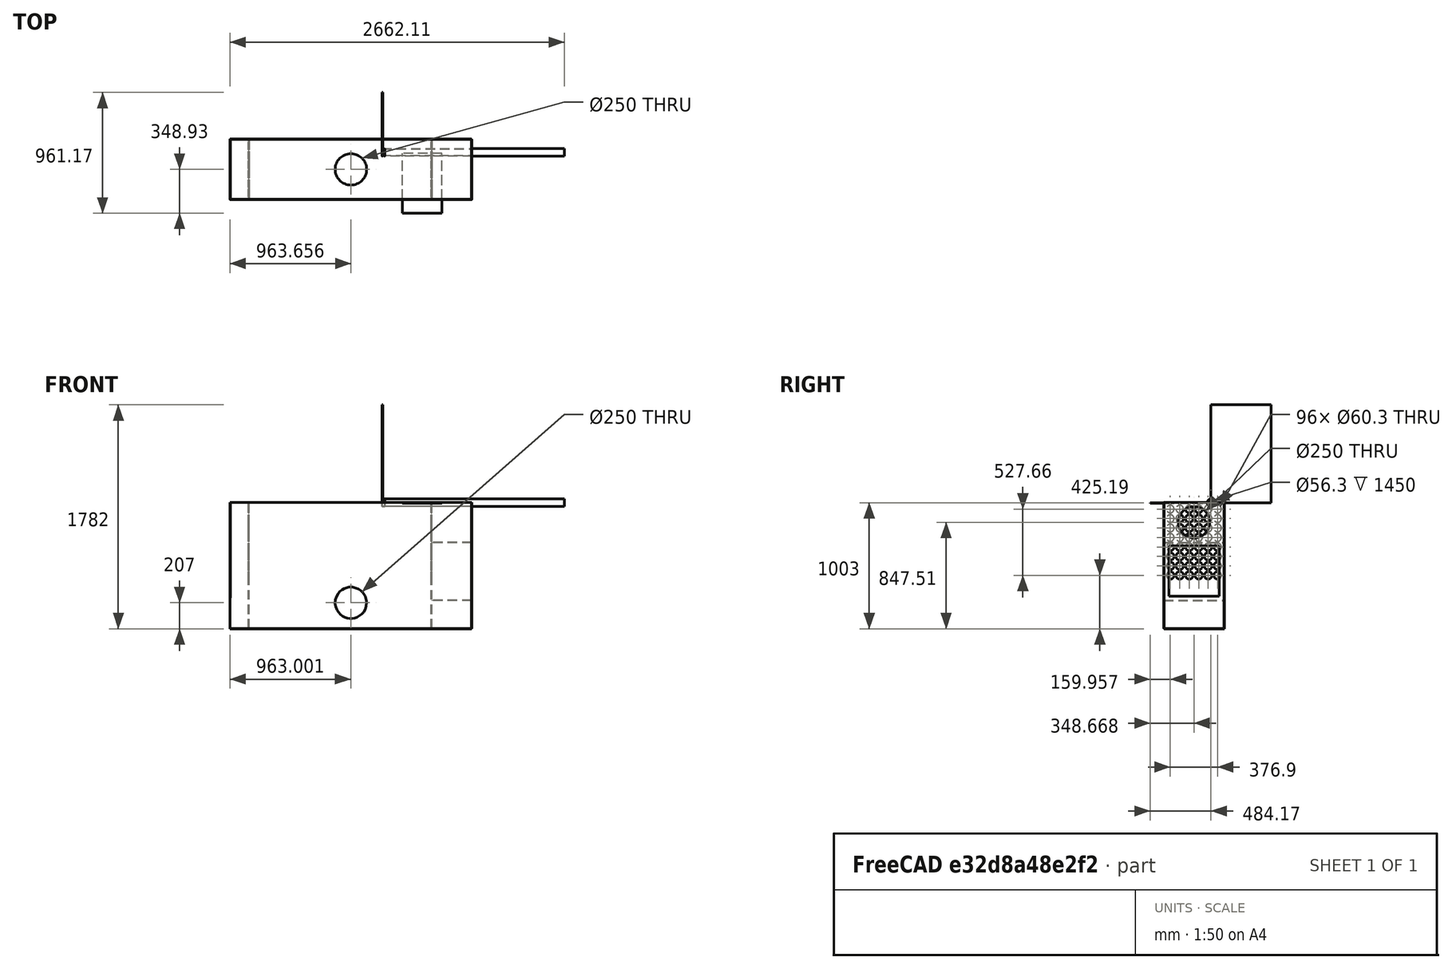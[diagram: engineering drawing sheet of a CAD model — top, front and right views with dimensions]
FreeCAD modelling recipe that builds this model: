
FCSTD DOCUMENT  (FreeCAD 0.19R24291 (Git))
Label: intercambiador_v5
License: All rights reserved
LicenseURL: http://en.wikipedia.org/wiki/All_rights_reserved
objects: TechDraw::DrawViewDimension×29, Part::Box×12, TechDraw::DrawViewPart×9, Part::Cylinder×7, Part::Cut×6, Part::Part2DObjectPython×6, TechDraw::DrawSVGTemplate×5, TechDraw::DrawPage×5, Part::FeaturePython×4, Part::RuledSurface×4, Part::Extrusion×4, Part::Refine×3, Part::MultiFuse×2, TechDraw::DrawHatch×2, Sketcher::SketchObject×1, PartDesign::Pad×1, PartDesign::Body×1
note: 48 computed .brp shape members not serialized (recipe doc carries the construction recipe); baked Part::Feature solids carry a one-line shape summary decoded from their .brp

FEATURE [Sketcher::SketchObject] Sketch
  FullyConstrained = false
  MapMode = 5
  Placement = pos=(0,0,0) rot=(0.57735,0.57735,0.57735;2.0944rad)
  Support = -> [YZ_Plane]
  sketch-geometry (2):
    g0: Circle CenterX=0 CenterY=0 CenterZ=0 NormalX=0 NormalY=0 NormalZ=1 AngleXU=0 Radius=30.15
    g1: Circle CenterX=0 CenterY=0 CenterZ=0 NormalX=0 NormalY=0 NormalZ=1 AngleXU=0 Radius=28.15
  constraints (2):
    c: Diameter(g0) = 60.3
    c: Diameter(g1) = 56.3
FEATURE [PartDesign::Pad] Pad
  AllowMultiFace = false
  Direction = (1,1,1)
  Length = 1450
  Length2 = 100
  Placement = pos=(0,0,0) rot=(0.57735,0.57735,0.57735;2.0944rad)
  Profile = -> Sketch
  Type = 0
FEATURE [PartDesign::Body] Body  label="Caño"
  Group = -> [Sketch,Pad]
  Origin = -> Origin
  Tip = -> Pad
FEATURE [Part::Cylinder] Cylinder  label="Cilindro"
  Angle = 360
  AttacherType = Attacher::AttachEngine3D
  Height = 20
  Placement = pos=(0,0,0) rot=(0,1,0;1.5708rad)
  Radius = 30.15
FEATURE [Part::Box] Box  label="Chapa tubos"
  AttacherType = Attacher::AttachEngine3D
  Height = 779
  Length = 6
  Width = 477
FEATURE [Part::Box] Box001  label="Placa separadora"
  AttacherType = Attacher::AttachEngine3D
  Height = 477
  Length = 3
  Placement = pos=(476.059,-484.167,0) rot=(0.57735,-0.57735,-0.57735;4.18879rad)
  Width = 314
FEATURE [Part::FeaturePython] Array  label="Banco tubos"  # Draft array (typed FeaturePython)
  Angle = 360
  ArrayType = 0
  Axis = (0,0,1)
  Base = -> Body
  Center = (0,0,0)
  Count = 48
  ExpandArray = false
  Fuse = false
  IntervalAxis = (0,0,0)
  IntervalX = (100,0,0)
  IntervalY = (0,75.38,0)
  IntervalZ = (0,0,75.38)
  NumberCircles = 3
  NumberPolar = 5
  NumberX = 1
  NumberY = 6
  NumberZ = 8
  Placement = pos=(-1053.11,-324.213,-577.81) rot=(0,0,1;0rad)
  PlacementList = 48 placements: [(0,0,0),(0,0,75.38),(0,0,150.76),(0,0,226.14),(0,0,301.52),(0,0,376.9),(0,0,452.28),(0,0,527.66),(0,75.38,0),(0,75.38,75.38),(0,75.38,150.76),(0,75.38,226.14),(0,75.38,301.52),(0,75.38,376.9),(0,75.38,452.28),(0,75.38,527.66),(0,150.76,0),(0,150.76,75.38),(0,150.76,150.76),(0,150.76,226.14),(0,150.76,301.52),(0,150.76,376.9),(0,150.76,452.28),(0,150.76,527.66),(0,226.14,0),(0,226.14,75.38),+22 more]
  RadialDistance = 50
  ScaleList = (48) [(1,1,1),(1,1,1),(1,1,1),(1,1,1),(1,1,1),(1,1,1),(1,1,1),(1,1,1),(1,1,1),(1,1,1),(1,1,1),(1,1,1),(1,1,1),(1,1,1),(1,1,1),(1,1,1),(1,1,1),(1,1,1),+30 more]
  Symmetry = 1
  TangentialDistance = 25
FEATURE [Part::Cylinder] Cylinder001  label="Cilindro001"
  Angle = 360
  AttacherType = Attacher::AttachEngine3D
  Height = 20
  Placement = pos=(0,0,0) rot=(0.707107,0,0.707107;3.14159rad)
  Radius = 30.15
FEATURE [Part::FeaturePython] Array002  label="Mach"  # Draft array (typed FeaturePython)
  Angle = 360
  ArrayType = 0
  Axis = (0,0,1)
  Base = -> Cylinder001
  Center = (0,0,0)
  Count = 48
  ExpandArray = false
  Fuse = false
  IntervalAxis = (0,0,0)
  IntervalX = (100,0,0)
  IntervalY = (0,75.38,0)
  IntervalZ = (0,0,75.38)
  NumberCircles = 3
  NumberPolar = 5
  NumberX = 1
  NumberY = 6
  NumberZ = 8
  Placement = pos=(-9,50.15,50.15) rot=(0,0,1;0rad)
  PlacementList = <same value as first occurrence — deduplicated (x4 in doc)>
  RadialDistance = 50
  ScaleList = (48) [(1,1,1),(1,1,1),(1,1,1),(1,1,1),(1,1,1),(1,1,1),(1,1,1),(1,1,1),(1,1,1),(1,1,1),(1,1,1),(1,1,1),(1,1,1),(1,1,1),(1,1,1),(1,1,1),(1,1,1),(1,1,1),+30 more]
  Symmetry = 1
  TangentialDistance = 25
FEATURE [Part::Box] Box002  label="Chapa tubos001"
  AttacherType = Attacher::AttachEngine3D
  Height = 779
  Length = 6
  Width = 477
FEATURE [Part::Cylinder] Cylinder002  label="Cilindro002"
  Angle = 360
  AttacherType = Attacher::AttachEngine3D
  Height = 20
  Placement = pos=(0,0,0) rot=(0.707107,0,0.707107;3.14159rad)
  Radius = 30.15
FEATURE [Part::FeaturePython] Array003  label="Mach001"  # Draft array (typed FeaturePython)
  Angle = 360
  ArrayType = 0
  Axis = (0,0,1)
  Base = -> Cylinder002
  Center = (0,0,0)
  Count = 48
  ExpandArray = false
  Fuse = false
  IntervalAxis = (0,0,0)
  IntervalX = (100,0,0)
  IntervalY = (0,75.38,0)
  IntervalZ = (0,0,75.38)
  NumberCircles = 3
  NumberPolar = 5
  NumberX = 1
  NumberY = 6
  NumberZ = 8
  Placement = pos=(-9,50.15,50.15) rot=(0,0,1;0rad)
  PlacementList = <same value as first occurrence — deduplicated (x4 in doc)>
  RadialDistance = 50
  ScaleList = (48) [(1,1,1),(1,1,1),(1,1,1),(1,1,1),(1,1,1),(1,1,1),(1,1,1),(1,1,1),(1,1,1),(1,1,1),(1,1,1),(1,1,1),(1,1,1),(1,1,1),(1,1,1),(1,1,1),(1,1,1),(1,1,1),+30 more]
  Symmetry = 1
  TangentialDistance = 25
FEATURE [Part::Cut] Cut001  label="Placa tubos 2"
  Base = -> Box002
  Placement = pos=(390.891,102.837,0) rot=(1,0,0;3.14159rad)
  Tool = -> Array003
FEATURE [Part::Box] Box003  label="Placa separadora_frente"
  AttacherType = Attacher::AttachEngine3D
  Height = 477
  Length = 3
  Placement = pos=(710.891,-374.263,-313.98) rot=(0.57735,-0.57735,-0.57735;4.18879rad)
  Width = 314
FEATURE [Part::Box] Box004  label="Placa separadora002"
  AttacherType = Attacher::AttachEngine3D
  Height = 477
  Length = 3
  Placement = pos=(476.059,-484.167,0) rot=(0.57735,-0.57735,-0.57735;4.18879rad)
  Width = 314
FEATURE [Part::Box] Box005  label="tapa"
  AttacherType = Attacher::AttachEngine3D
  Height = 477
  Length = 3
  Placement = pos=(711.546,-373.74,3) rot=(0.57735,-0.57735,-0.57735;4.18879rad)
  Width = 1920
FEATURE [Part::Part2DObjectPython] Line  # Draft 2D object (typed FeaturePython)
  Area = 0
  ChamferSize = 0
  Closed = false
  End = (396.891,-324.213,-577.81)
  FilletRadius = 0
  Length = 527.66
  MakeFace = false
  Placement = pos=(396.891,-324.213,-50.15) rot=(0,0,1;0rad)
  Points = (2) [(0,0,0),(0,-5.68434e-14,-527.66)]
  Start = (396.891,-324.213,-50.15)
  Subdivisions = 0
FEATURE [Part::Part2DObjectPython] Line001  # Draft 2D object (typed FeaturePython)
  Area = 0
  ChamferSize = 0
  Closed = false
  End = (396.891,52.687,-577.81)
  FilletRadius = 0
  Length = 527.66
  MakeFace = false
  Placement = pos=(396.891,52.687,-50.15) rot=(0,0,1;0rad)
  Points = (2) [(0,0,0),(0,-6.39488e-14,-527.66)]
  Start = (396.891,52.687,-50.15)
  Subdivisions = 0
FEATURE [Part::Part2DObjectPython] Line002  # Draft 2D object (typed FeaturePython)
  Area = 0
  ChamferSize = 0
  Closed = false
  End = (396.891,52.687,-313.98)
  FilletRadius = 0
  Length = 376.9
  MakeFace = false
  Placement = pos=(396.891,-324.213,-313.98) rot=(0,0,1;0rad)
  Points = (2) [(0,0,0),(0,376.9,-5.68434e-14)]
  Start = (396.891,-324.213,-313.98)
  Subdivisions = 0
FEATURE [Part::Box] Box006  label="Chapa tubos002"
  AttacherType = Attacher::AttachEngine3D
  Height = 779
  Length = 6
  Width = 477
FEATURE [Part::Cylinder] Cylinder003  label="Cilindro003"
  Angle = 360
  AttacherType = Attacher::AttachEngine3D
  Height = 20
  Placement = pos=(0,0,0) rot=(0.707107,0,0.707107;3.14159rad)
  Radius = 30.15
FEATURE [Part::FeaturePython] Array004  label="Mach002"  # Draft array (typed FeaturePython)
  Angle = 360
  ArrayType = 0
  Axis = (0,0,1)
  Base = -> Cylinder003
  Center = (0,0,0)
  Count = 48
  ExpandArray = false
  Fuse = false
  IntervalAxis = (0,0,0)
  IntervalX = (100,0,0)
  IntervalY = (0,75.38,0)
  IntervalZ = (0,0,75.38)
  NumberCircles = 3
  NumberPolar = 5
  NumberX = 1
  NumberY = 6
  NumberZ = 8
  Placement = pos=(-9,50.15,50.15) rot=(0,0,1;0rad)
  PlacementList = <same value as first occurrence — deduplicated (x4 in doc)>
  RadialDistance = 50
  ScaleList = (48) [(1,1,1),(1,1,1),(1,1,1),(1,1,1),(1,1,1),(1,1,1),(1,1,1),(1,1,1),(1,1,1),(1,1,1),(1,1,1),(1,1,1),(1,1,1),(1,1,1),(1,1,1),(1,1,1),(1,1,1),(1,1,1),+30 more]
  Symmetry = 1
  TangentialDistance = 25
FEATURE [Part::Cut] Cut002  label="Placa tubos 1"
  Base = -> Box006
  Placement = pos=(-1065.11,102.837,-4.55e-13) rot=(1,0,0;3.14159rad)
  Tool = -> Array004
FEATURE [Part::Box] Box007  label="Base"
  AttacherType = Attacher::AttachEngine3D
  Height = 477
  Length = 3
  Placement = pos=(710.891,-374.163,-1000) rot=(0.57735,-0.57735,-0.57735;4.18879rad)
  Width = 1920
FEATURE [Part::Box] Box008  label="Placa separadora003"
  AttacherType = Attacher::AttachEngine3D
  Height = 477
  Length = 3
  Placement = pos=(710.891,-374.163,-776) rot=(0.57735,-0.57735,-0.57735;4.18879rad)
  Width = 314
FEATURE [Part::RuledSurface] Ruled_Surface  label="lateral trasera"
  Curve1 = -> Box007 [Edge3]
  Curve2 = -> Box005 [Edge3]
  Orientation = 0
FEATURE [Part::RuledSurface] Ruled_Surface001
  Curve1 = -> Box005 [Edge4]
  Curve2 = -> Box007 [Edge4]
  Orientation = 0
FEATURE [Part::RuledSurface] Ruled_Surface002
  Curve1 = -> Box005 [Edge1]
  Curve2 = -> Box007 [Edge1]
  Orientation = 0
FEATURE [Part::RuledSurface] Ruled_Surface003
  Curve1 = -> Box007 [Edge6]
  Curve2 = -> Box005 [Edge6]
  Orientation = 0
FEATURE [Part::Extrusion] Extrude002  label="cabezal trasero"
  Base = -> Ruled_Surface
  Dir = (-1,0,0)
  DirMode = 0
  FaceMakerClass = Part::FaceMakerBullseye
  LengthFwd = 3
  LengthRev = 0
  Solid = false
  Symmetric = false
FEATURE [Part::Extrusion] Extrude  label="Lateral izq"
  Base = -> Ruled_Surface001
  Dir = (0,-1,0)
  DirMode = 0
  FaceMakerClass = Part::FaceMakerBullseye
  LengthFwd = 3
  LengthRev = 0
  Solid = false
  Symmetric = false
FEATURE [Part::Extrusion] Extrude004  label="Lateral der"
  Base = -> Ruled_Surface003
  Dir = (0,1,0)
  DirMode = 0
  FaceMakerClass = Part::FaceMakerBullseye
  LengthFwd = 3
  LengthRev = 0
  Solid = false
  Symmetric = false
FEATURE [Part::Cylinder] Cylinder006  label="Cilindro006"
  Angle = 360
  AttacherType = Attacher::AttachEngine3D
  Height = 60
  Placement = pos=(691.219,-135.501,-155.49) rot=(0,1,0;1.5708rad)
  Radius = 125
FEATURE [Part::Part2DObjectPython] Line003  # Draft 2D object (typed FeaturePython)
  Area = 0
  ChamferSize = 0
  Closed = false
  End = (710.891,-135.763,-313.98)
  FilletRadius = 0
  Length = 316.981
  MakeFace = false
  Placement = pos=(711.546,-135.24,3) rot=(0,0,1;0rad)
  Points = (2) [(0,0,0),(-0.655294,-0.52307,-316.98)]
  Start = (711.546,-135.24,3)
  Subdivisions = 0
FEATURE [Part::Box] Box009  label="Cubo"
  AttacherType = Attacher::AttachEngine3D
  Height = 400
  Length = 80
  Placement = pos=(650.891,-335.713,-744.99) rot=(0,0,1;0rad)
  Width = 400
FEATURE [Part::Part2DObjectPython] Line004  # Draft 2D object (typed FeaturePython)
  Area = 0
  ChamferSize = 0
  Closed = false
  End = (710.891,-135.663,-776)
  FilletRadius = 0
  Length = 462.02
  MakeFace = false
  Placement = pos=(710.891,-135.763,-313.98) rot=(0,0,1;0rad)
  Points = (2) [(0,0,0),(0,0.1,-462.02)]
  Start = (710.891,-135.763,-313.98)
  Subdivisions = 0
FEATURE [Part::Part2DObjectPython] Line005  # Draft 2D object (typed FeaturePython)
  Area = 0
  ChamferSize = 0
  Closed = false
  End = (-249.109,-377.163,-706)
  FilletRadius = 0
  Length = 70
  MakeFace = false
  Placement = pos=(-249.109,-377.163,-776) rot=(0,0,1;0rad)
  Points = (2) [(0,0,0),(0,0,70)]
  Start = (-249.109,-377.163,-776)
  Subdivisions = 0
FEATURE [Part::Cylinder] Cylinder007  label="Cilindro007"
  Angle = 360
  AttacherType = Attacher::AttachEngine3D
  Height = 70
  Placement = pos=(-249.109,-350.16,-796) rot=(1,0,0;1.5708rad)
  Radius = 125
FEATURE [Part::Cut] Cut004  label="lateral izq"
  Base = -> Extrude
  Tool = -> Cylinder007
FEATURE [Part::Cylinder] Cylinder008  label="Cilindro008"
  Angle = 360
  AttacherType = Attacher::AttachEngine3D
  Height = 60
  Placement = pos=(-248.454,-135.24,-50) rot=(0,0,1;1.5708rad)
  Radius = 125
FEATURE [Part::Cut] Cut005  label="Tapa"
  Base = -> Box005
  Tool = -> Cylinder008
FEATURE [TechDraw::DrawSVGTemplate] Template
  EditableTexts = APPROVER_NAME=APPROVER NAME,AUTHOR_NAME=AUTHOR NAME,DATE=YYYY-MM-DD,DN=DN,DOCUMENT_TYPE=Mechanical assembly drawing,OWNER_NAME=OWNER NAME,PM=PM,PN=PN,+7 more (map truncated)
  Height = 210
  Orientation = 1
  Width = 297
FEATURE [Part::Extrusion] Extrude003  label="cabezal frontal"
  Base = -> Ruled_Surface002
  Dir = (1,0,0)
  DirMode = 0
  FaceMakerClass = Part::FaceMakerBullseye
  LengthFwd = 3
  LengthRev = 0
  Solid = false
  Symmetric = false
FEATURE [Part::Cut] Cut
  Base = -> Extrude003
  Tool = -> Cylinder006
FEATURE [Part::Cut] Cut003  label="cabezal front"
  Base = -> Cut
  Tool = -> Box009
FEATURE [TechDraw::DrawViewPart] View  label="Cabezal Frontal"
  CoarseView = false
  Direction = (1,0,0)
  Focus = 100
  HardHidden = false
  IsoCount = 0
  IsoHidden = false
  IsoVisible = false
  LockPosition = false
  Perspective = false
  Rotation = 0
  Scale = 0.12
  ScaleType = 0
  SeamHidden = false
  SeamVisible = true
  SmoothHidden = false
  SmoothVisible = true
  Source = -> [Cut003]
  X = 52.7481
  XDirection = (0,1,0)
  Y = 114.029
FEATURE [TechDraw::DrawViewDimension] Dimension
  Arbitrary = false
  ArbitraryTolerances = false
  EqualTolerance = true
  FormatSpec = %.2f
  FormatSpecOverTolerance = %+.2f
  FormatSpecUnderTolerance = %+.2f
  Inverted = false
  LockPosition = false
  MeasureType = 1
  OverTolerance = 0
  References2D = -> [View]
  Rotation = 0
  ScaleType = 0
  TheoreticalExact = false
  Type = 1
  UnderTolerance = 0
  X = 0.846231
  Y = 68.7989
FEATURE [TechDraw::DrawViewDimension] Dimension001
  Arbitrary = false
  ArbitraryTolerances = false
  EqualTolerance = true
  FormatSpec = %.2f
  FormatSpecOverTolerance = %+.2f
  FormatSpecUnderTolerance = %+.2f
  Inverted = false
  LockPosition = false
  MeasureType = 1
  OverTolerance = 0
  References2D = -> [View]
  Rotation = 0
  ScaleType = 0
  TheoreticalExact = false
  Type = 2
  UnderTolerance = 0
  X = 36.418
  Y = 0
FEATURE [TechDraw::DrawViewDimension] Dimension002
  Arbitrary = false
  ArbitraryTolerances = false
  EqualTolerance = true
  FormatSpec = ⌀%.2f
  FormatSpecOverTolerance = %+.2f
  FormatSpecUnderTolerance = %+.2f
  Inverted = false
  LockPosition = false
  MeasureType = 1
  OverTolerance = 0
  References2D = -> [View]
  Rotation = 0
  ScaleType = 0
  TheoreticalExact = false
  Type = 5
  UnderTolerance = 0
  X = -1.64169
  Y = 46.3779
FEATURE [TechDraw::DrawViewDimension] Dimension003
  Arbitrary = false
  ArbitraryTolerances = false
  EqualTolerance = true
  FormatSpec = %.2f
  FormatSpecOverTolerance = %+.2f
  FormatSpecUnderTolerance = %+.2f
  Inverted = false
  LockPosition = false
  MeasureType = 1
  OverTolerance = 0
  References2D = -> [View]
  Rotation = 0
  ScaleType = 0
  TheoreticalExact = false
  Type = 1
  UnderTolerance = 0
  X = 0.789463
  Y = -35.3247
FEATURE [TechDraw::DrawViewDimension] Dimension004
  Arbitrary = false
  ArbitraryTolerances = false
  EqualTolerance = true
  FormatSpec = %.2f
  FormatSpecOverTolerance = %+.2f
  FormatSpecUnderTolerance = %+.2f
  Inverted = false
  LockPosition = false
  MeasureType = 1
  OverTolerance = 0
  References2D = -> [View]
  Rotation = 0
  ScaleType = 0
  TheoreticalExact = false
  Type = 2
  UnderTolerance = 0
  X = -40.4679
  Y = -7.63092
FEATURE [TechDraw::DrawSVGTemplate] Template001
  EditableTexts = AUTHOR_NAME=AUTHOR NAME,DN=DN,DRAWING_TITLE=DRAWING TITLE,FC-DATE=DD/MM/YYYY,FC-REV=REV A,FC-SC=SCALE,FC-SH=X / Y,FC-SI=A4,+2 more (map truncated)
  Height = 210
  Orientation = 1
  Width = 297
FEATURE [Part::Box] Box010  label="Cubo001"
  AttacherType = Attacher::AttachEngine3D
  Height = 221
  Length = 6
  Placement = pos=(390.891,-374.163,-1000) rot=(0,0,1;0rad)
  Width = 477
FEATURE [Part::MultiFuse] Fusion
  Shapes = -> [Cut001,Box010]
FEATURE [Part::Box] Box011  label="Cubo002"
  AttacherType = Attacher::AttachEngine3D
  Height = 221
  Length = 6
  Placement = pos=(-1065.11,-374.163,-1000) rot=(0,0,1;0rad)
  Width = 477
FEATURE [Part::MultiFuse] Fusion001
  Shapes = -> [Cut002,Box011]
FEATURE [Part::Refine] Fusion001001
  Source = -> Fusion001
FEATURE [Part::Refine] Fusion001002
  Source = -> Fusion
FEATURE [TechDraw::DrawViewPart] View004  label="Placa Porta Tubos"
  CoarseView = false
  Direction = (1,0,0)
  Focus = 100
  HardHidden = false
  IsoCount = 0
  IsoHidden = false
  IsoVisible = false
  LockPosition = false
  Perspective = false
  Rotation = 180
  Scale = 0.12
  ScaleType = 0
  SeamHidden = false
  SeamVisible = true
  SmoothHidden = false
  SmoothVisible = true
  Source = -> [Fusion001002,Box003]
  X = 147.737
  XDirection = (0,-1,0)
  Y = 113.009
FEATURE [TechDraw::DrawViewDimension] Dimension014
  Arbitrary = false
  ArbitraryTolerances = false
  EqualTolerance = true
  FormatSpec = %.2f
  FormatSpecOverTolerance = %+.2f
  FormatSpecUnderTolerance = %+.2f
  Inverted = false
  LockPosition = false
  MeasureType = 1
  OverTolerance = 0
  References2D = -> [View004]
  Rotation = 0
  ScaleType = 0
  TheoreticalExact = false
  Type = 2
  UnderTolerance = 0
  X = 39.5504
  Y = 0
FEATURE [TechDraw::DrawViewDimension] Dimension015
  Arbitrary = false
  ArbitraryTolerances = false
  EqualTolerance = true
  FormatSpec = %.2f
  FormatSpecOverTolerance = %+.2f
  FormatSpecUnderTolerance = %+.2f
  Inverted = false
  LockPosition = false
  MeasureType = 1
  OverTolerance = 0
  References2D = -> [View004]
  Rotation = 0
  ScaleType = 0
  TheoreticalExact = false
  Type = 1
  UnderTolerance = 0
  X = 0.006
  Y = 68.7713
FEATURE [TechDraw::DrawViewDimension] Dimension016
  Arbitrary = false
  ArbitraryTolerances = false
  EqualTolerance = true
  FormatSpec = ⌀%.2f
  FormatSpecOverTolerance = %+.2f
  FormatSpecUnderTolerance = %+.2f
  Inverted = false
  LockPosition = false
  MeasureType = 1
  OverTolerance = 0
  References2D = -> [View004]
  Rotation = 0
  ScaleType = 0
  TheoreticalExact = false
  Type = 5
  UnderTolerance = 0
  X = -37.7549
  Y = 41.5685
FEATURE [TechDraw::DrawViewDimension] Dimension017
  Arbitrary = false
  ArbitraryTolerances = false
  EqualTolerance = true
  FormatSpec = %.2f
  FormatSpecOverTolerance = %+.2f
  FormatSpecUnderTolerance = %+.2f
  Inverted = false
  LockPosition = false
  MeasureType = 1
  OverTolerance = 0
  References2D = -> [View004]
  Rotation = 0
  ScaleType = 0
  TheoreticalExact = false
  Type = 2
  UnderTolerance = 0
  X = -38.1541
  Y = -16.7306
FEATURE [TechDraw::DrawViewDimension] Dimension018
  Arbitrary = false
  ArbitraryTolerances = false
  EqualTolerance = true
  FormatSpec = %.2f
  FormatSpecOverTolerance = %+.2f
  FormatSpecUnderTolerance = %+.2f
  Inverted = false
  LockPosition = false
  MeasureType = 1
  OverTolerance = 0
  References2D = -> [View004]
  Rotation = 0
  ScaleType = 0
  TheoreticalExact = false
  Type = 2
  UnderTolerance = 0
  X = 34.3625
  Y = 32.5593
FEATURE [TechDraw::DrawViewPart] View005  label="Placa Porta Tubos Trasera"
  CoarseView = false
  Direction = (-1,0,0)
  Focus = 100
  HardHidden = false
  IsoCount = 0
  IsoHidden = false
  IsoVisible = false
  LockPosition = false
  Perspective = false
  Rotation = 0
  Scale = 0.12
  ScaleType = 0
  SeamHidden = false
  SeamVisible = true
  SmoothHidden = false
  SmoothVisible = true
  Source = -> [Fusion001002]
  X = 242.45
  XDirection = (0,-1,0)
  Y = 113.588
FEATURE [TechDraw::DrawViewDimension] Dimension019
  Arbitrary = false
  ArbitraryTolerances = false
  EqualTolerance = true
  FormatSpec = %.2f
  FormatSpecOverTolerance = %+.2f
  FormatSpecUnderTolerance = %+.2f
  Inverted = false
  LockPosition = false
  MeasureType = 1
  OverTolerance = 0
  References2D = -> [View005]
  Rotation = 0
  ScaleType = 0
  TheoreticalExact = false
  Type = 1
  UnderTolerance = 0
  X = -3.76556
  Y = -18.1602
FEATURE [TechDraw::DrawViewDimension] Dimension020
  Arbitrary = false
  ArbitraryTolerances = false
  EqualTolerance = true
  FormatSpec = %.2f
  FormatSpecOverTolerance = %+.2f
  FormatSpecUnderTolerance = %+.2f
  Inverted = false
  LockPosition = false
  MeasureType = 1
  OverTolerance = 0
  References2D = -> [View005]
  Rotation = 0
  ScaleType = 0
  TheoreticalExact = false
  Type = 2
  UnderTolerance = 0
  X = 35.1179
  Y = -17.8013
FEATURE [TechDraw::DrawViewPart] View006  label="Lateral Izquierdo"
  CoarseView = false
  Direction = (0,-1,0)
  Focus = 100
  HardHidden = false
  IsoCount = 0
  IsoHidden = false
  IsoVisible = false
  LockPosition = false
  Perspective = false
  Rotation = 0
  Scale = 0.12
  ScaleType = 0
  SeamHidden = false
  SeamVisible = true
  SmoothHidden = false
  SmoothVisible = true
  Source = -> [Extrude002,Extrude004,Box003,Cut003,Cut005,Fusion001001,Fusion001002,Array,Box007]
  X = 147.032
  XDirection = (1,0,0)
  Y = 118.319
FEATURE [TechDraw::DrawViewDimension] Dimension022
  Arbitrary = false
  ArbitraryTolerances = false
  EqualTolerance = true
  FormatSpec = %.2f
  FormatSpecOverTolerance = %+.2f
  FormatSpecUnderTolerance = %+.2f
  Inverted = false
  LockPosition = false
  MeasureType = 1
  OverTolerance = 0
  References2D = -> [View006]
  Rotation = 0
  Scale = 0.12
  ScaleType = 0
  TheoreticalExact = false
  Type = 2
  UnderTolerance = 0
  X = 127.538
  Y = -20.0794
FEATURE [TechDraw::DrawViewDimension] Dimension023
  Arbitrary = false
  ArbitraryTolerances = false
  EqualTolerance = true
  FormatSpec = %.2f
  FormatSpecOverTolerance = %+.2f
  FormatSpecUnderTolerance = %+.2f
  Inverted = false
  LockPosition = false
  MeasureType = 1
  OverTolerance = 0
  References2D = -> [View006]
  Rotation = 0
  Scale = 0.12
  ScaleType = 0
  TheoreticalExact = false
  Type = 2
  UnderTolerance = 0
  X = 127.927
  Y = 37.7994
FEATURE [TechDraw::DrawViewDimension] Dimension024
  Arbitrary = false
  ArbitraryTolerances = false
  EqualTolerance = true
  FormatSpec = %.2f
  FormatSpecOverTolerance = %+.2f
  FormatSpecUnderTolerance = %+.2f
  Inverted = false
  LockPosition = false
  MeasureType = 1
  OverTolerance = 0
  References2D = -> [View006]
  Rotation = 0
  Scale = 0.12
  ScaleType = 0
  TheoreticalExact = false
  Type = 2
  UnderTolerance = 0
  X = -130.673
  Y = 24.3615
FEATURE [TechDraw::DrawViewDimension] Dimension026
  Arbitrary = false
  ArbitraryTolerances = false
  EqualTolerance = true
  FormatSpec = %.2f
  FormatSpecOverTolerance = %+.2f
  FormatSpecUnderTolerance = %+.2f
  Inverted = false
  LockPosition = false
  MeasureType = 1
  OverTolerance = 0
  References2D = -> [View006]
  Rotation = 0
  Scale = 0.12
  ScaleType = 0
  TheoreticalExact = false
  Type = 1
  UnderTolerance = 0
  X = -8.35003
  Y = 68.305
FEATURE [TechDraw::DrawViewDimension] Dimension027
  Arbitrary = false
  ArbitraryTolerances = false
  EqualTolerance = true
  FormatSpec = %.2f
  FormatSpecOverTolerance = %+.2f
  FormatSpecUnderTolerance = %+.2f
  Inverted = false
  LockPosition = false
  MeasureType = 1
  OverTolerance = 0
  References2D = -> [View006]
  Rotation = 0
  Scale = 0.12
  ScaleType = 0
  TheoreticalExact = false
  Type = 1
  UnderTolerance = 0
  X = 57.9191
  Y = -42.6681
FEATURE [TechDraw::DrawViewDimension] Dimension028
  Arbitrary = false
  ArbitraryTolerances = false
  EqualTolerance = true
  FormatSpec = %.2f
  FormatSpecOverTolerance = %+.2f
  FormatSpecUnderTolerance = %+.2f
  Inverted = false
  LockPosition = false
  MeasureType = 1
  OverTolerance = 0
  References2D = -> [View006]
  Rotation = 0
  Scale = 0.12
  ScaleType = 0
  TheoreticalExact = false
  Type = 1
  UnderTolerance = 0
  X = -106.239
  Y = -61.7093
FEATURE [TechDraw::DrawViewDimension] Dimension029
  Arbitrary = false
  ArbitraryTolerances = false
  EqualTolerance = true
  FormatSpec = %.2f
  FormatSpecOverTolerance = %+.2f
  FormatSpecUnderTolerance = %+.2f
  Inverted = false
  LockPosition = false
  MeasureType = 1
  OverTolerance = 0
  References2D = -> [View006]
  Rotation = 0
  Scale = 0.12
  ScaleType = 0
  TheoreticalExact = false
  Type = 1
  UnderTolerance = 0
  X = 98.5488
  Y = 68.666
FEATURE [TechDraw::DrawSVGTemplate] Template003
  EditableTexts = AUTHOR_NAME=AUTHOR NAME; DN=DN; DRAWING_TITLE=Panel Lateral; FC-DATE=DD/MM/YYYY; FC-REV=REV A; FC-SC=1:8; FC-SH=X / Y; FC-SI=A4; FreeCAD_DRAWING=Lateral; PN=PN
  Height = 210
  Orientation = 1
  Width = 297
FEATURE [TechDraw::DrawViewPart] View008
  CoarseView = false
  Direction = (0,-1,0)
  Focus = 100
  HardHidden = false
  IsoCount = 0
  IsoHidden = false
  IsoVisible = false
  LockPosition = false
  Perspective = false
  Rotation = 0
  Scale = 0.12
  ScaleType = 0
  SeamHidden = false
  SeamVisible = true
  SmoothHidden = false
  SmoothVisible = true
  Source = -> [Cut004,Extrude004]
  X = 151.578
  XDirection = (1,0,0)
  Y = 122.101
FEATURE [Part::Refine] Cut004001001  label="lateral izq002"
FEATURE [TechDraw::DrawSVGTemplate] Template004
  EditableTexts = AUTHOR_NAME=AUTHOR NAME,DN=DN,DRAWING_TITLE=DRAWING TITLE,FC-DATE=DD/MM/YYYY,FC-REV=REV A,FC-SC=1:8,FC-SH=X / Y,FC-SI=A3,+2 more (map truncated)
  Height = 297
  Orientation = 1
  Width = 420
FEATURE [TechDraw::DrawViewPart] View009  label="Intercambiador conjunto"
  CoarseView = false
  Direction = (0.577,-0.577,0.577)
  Focus = 100
  HardHidden = false
  IsoCount = 0
  IsoHidden = false
  IsoVisible = false
  LockPosition = false
  Perspective = false
  Rotation = 0
  Scale = 0.1
  ScaleType = 0
  SeamHidden = false
  SeamVisible = true
  SmoothHidden = false
  SmoothVisible = true
  Source = -> [Cut005,Cut004,Cut003,Extrude004,Box007,Extrude002,Array,Box003,Fusion001001,Fusion001002]
  X = 316.417
  XDirection = (0.707,0.707,0)
  Y = 190.099
FEATURE [TechDraw::DrawViewPart] View010  label="Intercambiador abierto"
  CoarseView = false
  Direction = (0.82,0.511,0.259)
  Focus = 100
  HardHidden = false
  IsoCount = 0
  IsoHidden = false
  IsoVisible = false
  LockPosition = false
  Perspective = false
  Rotation = 0
  Scale = 0.1
  ScaleType = 0
  SeamHidden = false
  SeamVisible = true
  SmoothHidden = false
  SmoothVisible = true
  Source = -> [Array,Box003,Extrude002,Box007,Cut003,Cut004,Cut005,Fusion001001,Fusion001002]
  X = 118.96
  XDirection = (-0.531,0.847,0.009)
  Y = 185.314
FEATURE [TechDraw::DrawPage] Page004  label="Equipo"
  KeepUpdated = true
  NextBalloonIndex = 1
  ProjectionType = 0
  Template = -> Template004
  Views = -> [View009,View010]
FEATURE [TechDraw::DrawSVGTemplate] Template005
  EditableTexts = AUTHOR_NAME=AUTHOR NAME; DN=DN; DRAWING_TITLE=Banco de Tubos; FC-DATE=DD/MM/YYYY; FC-REV=REV A; FC-SC=1:8; FC-SH=X / Y; FC-SI=A4; FreeCAD_DRAWING=Banco de Tubos; PN=PN
  Height = 210
  Orientation = 1
  Width = 297
FEATURE [TechDraw::DrawViewPart] View011  label="Banco Tubos frente"
  CoarseView = false
  Direction = (-1,0,0)
  Focus = 100
  HardHidden = false
  IsoCount = 0
  IsoHidden = false
  IsoVisible = false
  LockPosition = false
  Perspective = false
  Rotation = 0
  Scale = 0.12
  ScaleType = 0
  SeamHidden = false
  SeamVisible = true
  SmoothHidden = false
  SmoothVisible = true
  Source = -> [Array]
  X = 57.5816
  XDirection = (0,-1,0)
  Y = 139.798
FEATURE [TechDraw::DrawViewDimension] Dimension030
  Arbitrary = false
  ArbitraryTolerances = false
  EqualTolerance = true
  FormatSpec = ⌀%.2f
  FormatSpecOverTolerance = %+.2f
  FormatSpecUnderTolerance = %+.2f
  Inverted = false
  LockPosition = false
  MeasureType = 1
  OverTolerance = 0
  References2D = -> [View011]
  Rotation = 0
  ScaleType = 0
  TheoreticalExact = false
  Type = 5
  UnderTolerance = 0
  X = 33.226
  Y = 37.4629
FEATURE [TechDraw::DrawViewDimension] Dimension031
  Arbitrary = false
  ArbitraryTolerances = false
  EqualTolerance = true
  FormatSpec = ⌀%.2f
  FormatSpecOverTolerance = %+.2f
  FormatSpecUnderTolerance = %+.2f
  Inverted = false
  LockPosition = false
  MeasureType = 1
  OverTolerance = 0
  References2D = -> [View011]
  Rotation = 0
  ScaleType = 0
  TheoreticalExact = false
  Type = 5
  UnderTolerance = 0
  X = -38.5332
  Y = 37.1953
FEATURE [TechDraw::DrawViewDimension] Dimension032
  Arbitrary = false
  ArbitraryTolerances = false
  EqualTolerance = true
  FormatSpec = %.2f
  FormatSpecOverTolerance = %+.2f
  FormatSpecUnderTolerance = %+.2f
  Inverted = false
  LockPosition = false
  MeasureType = 1
  OverTolerance = 0
  References2D = -> [View011]
  Rotation = 0
  ScaleType = 0
  TheoreticalExact = false
  Type = 1
  UnderTolerance = 0
  X = -10.4605
  Y = 45.3099
FEATURE [TechDraw::DrawViewPart] View012  label="Banco Tubos Lateral"
  CoarseView = false
  Direction = (0,1,0)
  Focus = 100
  HardHidden = false
  IsoCount = 0
  IsoHidden = false
  IsoVisible = false
  LockPosition = false
  Perspective = false
  Rotation = 0
  Scale = 0.12
  ScaleType = 0
  SeamHidden = false
  SeamVisible = true
  SmoothHidden = false
  SmoothVisible = true
  Source = -> [Array]
  X = 193.726
  XDirection = (-1,0,0)
  Y = 141.684
FEATURE [TechDraw::DrawViewDimension] Dimension033
  Arbitrary = false
  ArbitraryTolerances = false
  EqualTolerance = true
  FormatSpec = %.2f
  FormatSpecOverTolerance = %+.2f
  FormatSpecUnderTolerance = %+.2f
  Inverted = false
  LockPosition = false
  MeasureType = 1
  OverTolerance = 0
  References2D = -> [View012]
  Rotation = 0
  ScaleType = 0
  TheoreticalExact = false
  Type = 2
  UnderTolerance = 0
  X = -95.3881
  Y = -9.69083
FEATURE [TechDraw::DrawViewDimension] Dimension034
  Arbitrary = false
  ArbitraryTolerances = false
  EqualTolerance = true
  FormatSpec = %.2f
  FormatSpecOverTolerance = %+.2f
  FormatSpecUnderTolerance = %+.2f
  Inverted = false
  LockPosition = false
  MeasureType = 1
  OverTolerance = 0
  References2D = -> [View012]
  Rotation = 0
  ScaleType = 0
  TheoreticalExact = false
  Type = 1
  UnderTolerance = 0
  X = -0.802776
  Y = 45.4461
FEATURE [TechDraw::DrawPage] Page005  label="Banco Tubos"
  KeepUpdated = true
  NextBalloonIndex = 1
  ProjectionType = 0
  Template = -> Template005
  Views = -> [View011,View012,Dimension030,Dimension031,Dimension032,Dimension033,Dimension034]
FEATURE [TechDraw::DrawViewDimension] Dimension035
  Arbitrary = false
  ArbitraryTolerances = false
  EqualTolerance = true
  FormatSpec = %.2f
  FormatSpecOverTolerance = %+.2f
  FormatSpecUnderTolerance = %+.2f
  Inverted = false
  LockPosition = false
  MeasureType = 1
  OverTolerance = 0
  References2D = -> [View008]
  Rotation = 0
  ScaleType = 0
  TheoreticalExact = false
  Type = 1
  UnderTolerance = 0
  X = -1.36783
  Y = 48.9237
FEATURE [TechDraw::DrawViewDimension] Dimension036
  Arbitrary = false
  ArbitraryTolerances = false
  EqualTolerance = true
  FormatSpec = ⌀%.2f
  FormatSpecOverTolerance = %+.2f
  FormatSpecUnderTolerance = %+.2f
  Inverted = false
  LockPosition = false
  MeasureType = 1
  OverTolerance = 0
  References2D = -> [View008]
  Rotation = 0
  ScaleType = 0
  TheoreticalExact = false
  Type = 5
  UnderTolerance = 0
  X = -28.8442
  Y = -30.2513
FEATURE [TechDraw::DrawViewDimension] Dimension037
  Arbitrary = false
  ArbitraryTolerances = false
  EqualTolerance = true
  FormatSpec = %.2f
  FormatSpecOverTolerance = %+.2f
  FormatSpecUnderTolerance = %+.2f
  Inverted = false
  LockPosition = false
  MeasureType = 1
  OverTolerance = 0
  References2D = -> [View008]
  Rotation = 0
  ScaleType = 0
  TheoreticalExact = false
  Type = 2
  UnderTolerance = 0
  X = -126.808
  Y = -1.93055
FEATURE [TechDraw::DrawPage] Page003  label="Vista Lateral 2"
  KeepUpdated = true
  NextBalloonIndex = 1
  ProjectionType = 0
  Template = -> Template003
  Views = -> [View008,Dimension035,Dimension036,Dimension037]
FEATURE [TechDraw::DrawHatch] Hatch  label="HatchF0"
  HatchPattern = C:/Program Files/FreeCAD 0.19/data/Mod/TechDraw/Patterns/simple.svg
  Source = -> View [Face0]
FEATURE [TechDraw::DrawHatch] Hatch001  label="Hatch001F1"
  HatchPattern = C:/Program Files/FreeCAD 0.19/data/Mod/TechDraw/Patterns/simple.svg
  Source = -> View004 [Face1]
FEATURE [TechDraw::DrawViewDimension] Dimension038
  Arbitrary = false
  ArbitraryTolerances = false
  EqualTolerance = true
  FormatSpec = %.2f
  FormatSpecOverTolerance = %+.2f
  FormatSpecUnderTolerance = %+.2f
  Inverted = false
  LockPosition = false
  MeasureType = 1
  OverTolerance = 0
  References2D = -> [View004]
  Rotation = 0
  ScaleType = 0
  TheoreticalExact = false
  Type = 1
  UnderTolerance = 0
  X = 27.1679
  Y = 74.4882
FEATURE [TechDraw::DrawPage] Page  label="Vistas frontales"
  KeepUpdated = true
  NextBalloonIndex = 1
  ProjectionType = 0
  Template = -> Template
  Views = -> [View,Dimension,Dimension001,Dimension002,Dimension003,Dimension004,View004,Dimension014,Dimension015,Dimension016,Dimension017,Dimension018,View005,Dimension019,Dimension020,Dimension038]
FEATURE [TechDraw::DrawViewDimension] Dimension039
  Arbitrary = false
  ArbitraryTolerances = false
  EqualTolerance = true
  FormatSpec = %.2f
  FormatSpecOverTolerance = %+.2f
  FormatSpecUnderTolerance = %+.2f
  Inverted = false
  LockPosition = false
  MeasureType = 1
  OverTolerance = 0
  References2D = -> [View006]
  Rotation = 0
  Scale = 0.12
  ScaleType = 0
  TheoreticalExact = false
  Type = 2
  UnderTolerance = 0
  X = 120.06
  Y = 17.1617
FEATURE [TechDraw::DrawPage] Page001  label="Vista Lateral 1"
  KeepUpdated = true
  NextBalloonIndex = 1
  ProjectionType = 0
  Scale = 0.12
  Template = -> Template001
  Views = -> [View006,Dimension022,Dimension023,Dimension024,Dimension026,Dimension027,Dimension028,Dimension029,Dimension039]
